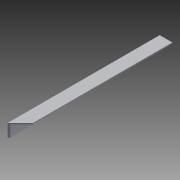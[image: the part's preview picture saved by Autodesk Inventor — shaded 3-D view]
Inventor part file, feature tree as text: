
AUTODESK INVENTOR PART (.ipt)
format: ipt  version: 2014 (Build 180170000, 170)  size: 82,432 bytes
history: native  units: in
note: dims shown in document units (in); Inventor stores cm internally (conversion verified against a paired STEP export)
features: extrude x2, sketch x2
ambient origin geometry x8: Origin, YZ Plane, XZ Plane, XY Plane, X Axis, Y Axis, Z Axis, Center Point
bodies: Solid1 (feature_tree)
feature tree (4):
  extrude  "Extrusion1"  Depth=0.5in
  extrude  "Extrusion3"  Depth=0.45in
  sketch  "Sketch1"  dims[d0=0.5in d1=0.5in]
  sketch  "Sketch3"  dims[d2=0.05in d3=0.45in d4=6.0in d5=0.0in d10=45.0deg d11=1.0in d12=0.0in]
